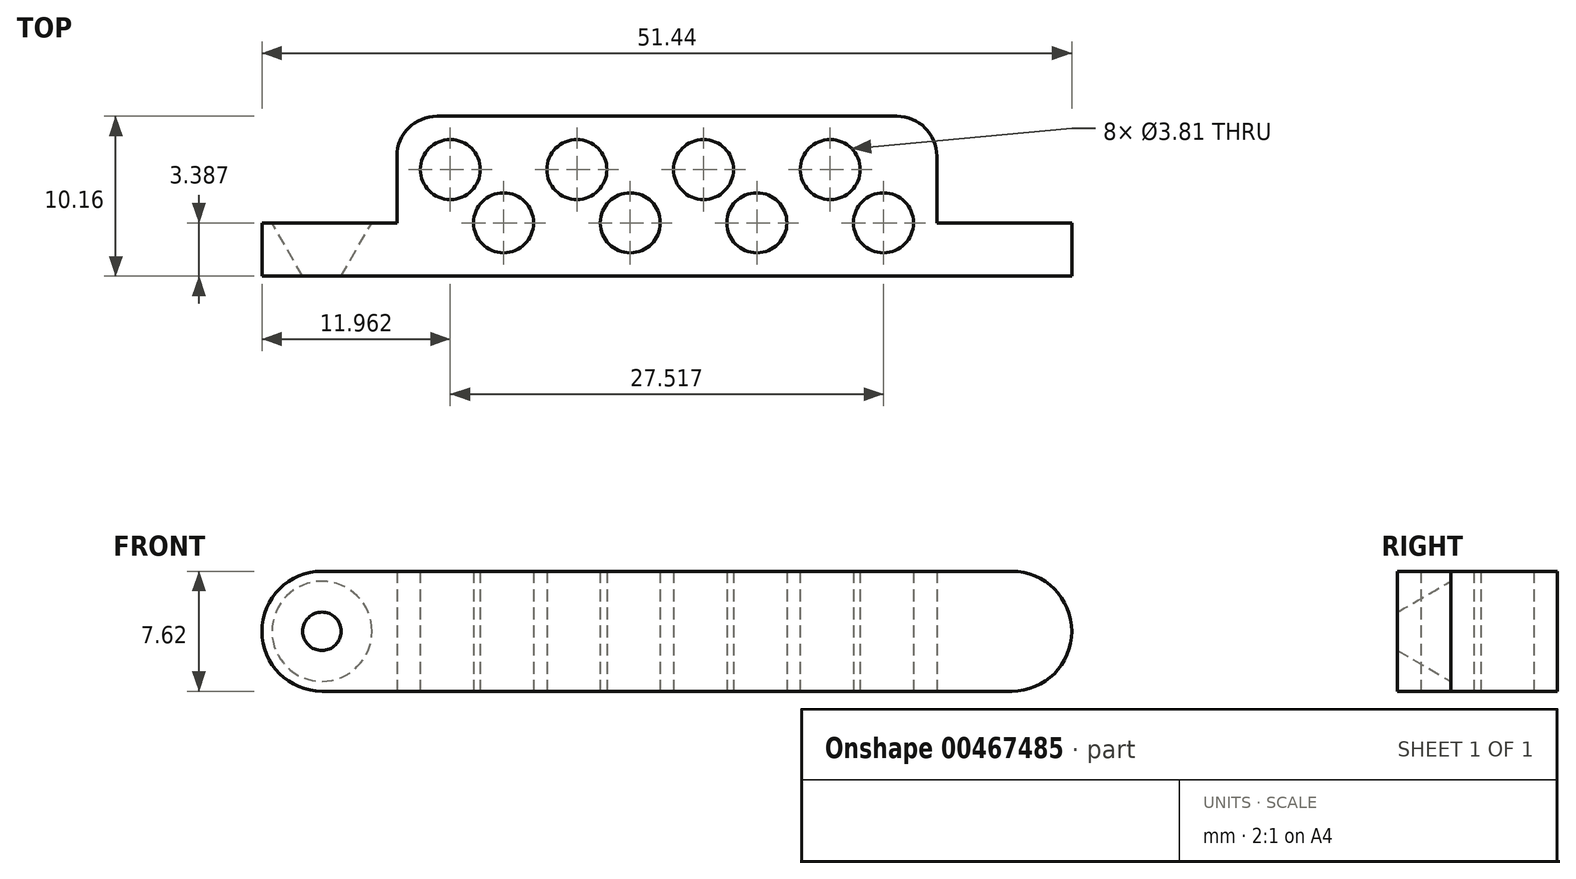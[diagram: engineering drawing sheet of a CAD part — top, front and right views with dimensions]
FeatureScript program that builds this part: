
annotation { "Feature Type Name" : "Feature", "Feature Type Description" : "" }
export const myFeature = defineFeature(function(context is Context, id is Id, definition is map)
    precondition{}
    {
        {
            var Q0;
            Q0=qCreatedBy(makeId("Top.planeOp"),FACE);
            var sketch = newSketch(context, id + "F0", { "sketchPlane" : qUnion([Q0])});
            skLineSegment(sketch, "E0", {"start": v(0, 10.16) * mm, "end": v(-17.15, 10.16) * mm});
            skLineSegment(sketch, "E1", {"start": v(-17.15, 10.16) * mm, "end": v(-17.14, 3.39) * mm});
            skLineSegment(sketch, "E2", {"start": v(-17.14, 3.39) * mm, "end": v(-25.72, 3.39) * mm});
            skLineSegment(sketch, "E3", {"start": v(-25.72, 3.39) * mm, "end": v(-25.72, 0) * mm});
            skLineSegment(sketch, "E4", {"start": v(-25.72, 0) * mm, "end": v(0, 0) * mm});
            skLineSegment(sketch, "E5.MirrorCS", {"start": v(25.72, 0) * mm, "end": v(0, 0) * mm});
            skLineSegment(sketch, "E6.MirrorCS", {"start": v(25.72, 3.39) * mm, "end": v(25.72, 0) * mm});
            skLineSegment(sketch, "E7.MirrorCS", {"start": v(17.14, 3.39) * mm, "end": v(25.72, 3.39) * mm});
            skLineSegment(sketch, "E8.MirrorCS", {"start": v(0, 10.16) * mm, "end": v(17.15, 10.16) * mm});
            skLineSegment(sketch, "E9.MirrorCS", {"start": v(17.14, 10.16) * mm, "end": v(17.14, 3.39) * mm});
            skSolve(sketch);
        }
        {
            var Q0;
            Q0 = qSketchRegion(id + "F0", true);
            extrude(context, id + "F1", {"entities" : qUnion([Q0]), "endBound" : BoundingType.SYMMETRIC, "depth" : 7.62 * mm});
        }
        {
            var Q0;
            Q0=qCreatedBy(makeId("Top.planeOp"),FACE);
            var sketch = newSketch(context, id + "F2", { "sketchPlane" : qUnion([Q0])});
            skCircle(sketch, "E10", {"center": v(-13.76, 6.77) * mm, "radius": 1.9 * mm});
            skCircle(sketch, "E11", {"center": v(-10.37, 3.39) * mm, "radius": 1.9 * mm});
            skLineSegment(sketch, "E12.0", {"start": v(-17.15, 10.16) * mm, "end": v(17.15, 10.16) * mm, "construction": true});
            skLineSegment(sketch, "E13.0", {"start": v(-17.15, 10.16) * mm, "end": v(-17.14, 3.39) * mm, "construction": true});
            skPoint(sketch, "E14", {"position": v(-13.76, 10.16) * mm});
            skLineSegment(sketch, "E15", {"start": v(-13.76, 6.77) * mm, "end": v(-13.76, 10.16) * mm, "construction": true});
            skLineSegment(sketch, "E16", {"start": v(-10.37, 3.39) * mm, "end": v(-10.37, 0) * mm, "construction": true});
            skLineSegment(sketch, "E17", {"start": v(-13.76, 6.77) * mm, "end": v(-13.76, 3.39) * mm, "construction": true});
            skLineSegment(sketch, "E18", {"start": v(-10.37, 3.39) * mm, "end": v(-13.76, 6.77) * mm, "construction": true});
            skPoint(sketch, "E19", {"position": v(-12.06, 5.08) * mm});
            skCircle(sketch, "E20.1.0.0", {"center": v(-2.33, 3.39) * mm, "radius": 1.9 * mm});
            skPoint(sketch, "E20.1.0.1", {"position": v(-5.72, 10.16) * mm});
            skLineSegment(sketch, "E20.1.0.2", {"start": v(-5.72, 6.77) * mm, "end": v(-5.71, 3.39) * mm, "construction": true});
            skLineSegment(sketch, "E20.1.0.3", {"start": v(-2.33, 3.39) * mm, "end": v(-5.72, 6.77) * mm, "construction": true});
            skPoint(sketch, "E20.1.0.4", {"position": v(-4.02, 5.08) * mm});
            skCircle(sketch, "E20.1.0.5", {"center": v(-5.72, 6.77) * mm, "radius": 1.9 * mm});
            skLineSegment(sketch, "E20.1.0.6", {"start": v(-2.33, 3.39) * mm, "end": v(-2.33, 0) * mm, "construction": true});
            skLineSegment(sketch, "E20.1.0.7", {"start": v(-5.71, 6.77) * mm, "end": v(-5.72, 10.16) * mm, "construction": true});
            skCircle(sketch, "E20.2.0.0", {"center": v(5.72, 3.39) * mm, "radius": 1.9 * mm});
            skPoint(sketch, "E20.2.0.1", {"position": v(2.33, 10.16) * mm});
            skLineSegment(sketch, "E20.2.0.2", {"start": v(2.33, 6.77) * mm, "end": v(2.33, 3.39) * mm, "construction": true});
            skLineSegment(sketch, "E20.2.0.3", {"start": v(5.72, 3.39) * mm, "end": v(2.33, 6.77) * mm, "construction": true});
            skPoint(sketch, "E20.2.0.4", {"position": v(4.02, 5.08) * mm});
            skCircle(sketch, "E20.2.0.5", {"center": v(2.33, 6.77) * mm, "radius": 1.9 * mm});
            skLineSegment(sketch, "E20.2.0.6", {"start": v(5.72, 3.39) * mm, "end": v(5.72, 0) * mm, "construction": true});
            skLineSegment(sketch, "E20.2.0.7", {"start": v(2.33, 6.77) * mm, "end": v(2.33, 10.16) * mm, "construction": true});
            skLineSegment(sketch, "E20.direction1", {"start": v(-10.37, 0) * mm, "end": v(-2.33, 0) * mm, "construction": true});
            skCircle(sketch, "E21.0.3.0", {"center": v(13.76, 3.39) * mm, "radius": 1.9 * mm});
            skPoint(sketch, "E21.2.3.0", {"position": v(10.37, 10.16) * mm});
            skLineSegment(sketch, "E21.3.3.0", {"start": v(10.37, 6.77) * mm, "end": v(10.37, 3.39) * mm, "construction": true});
            skLineSegment(sketch, "E21.6.3.0", {"start": v(13.76, 3.39) * mm, "end": v(10.37, 6.77) * mm, "construction": true});
            skPoint(sketch, "E21.9.3.0", {"position": v(12.06, 5.08) * mm});
            skCircle(sketch, "E21.10.3.0", {"center": v(10.37, 6.77) * mm, "radius": 1.9 * mm});
            skLineSegment(sketch, "E21.12.3.0", {"start": v(13.76, 3.39) * mm, "end": v(13.76, 0) * mm, "construction": true});
            skLineSegment(sketch, "E21.15.3.0", {"start": v(10.37, 6.77) * mm, "end": v(10.37, 10.16) * mm, "construction": true});
            skLineSegment(sketch, "E22", {"start": v(-12.06, 5.08) * mm, "end": v(-4.02, 5.08) * mm, "construction": true});
            skLineSegment(sketch, "E23", {"start": v(4.02, 5.08) * mm, "end": v(-4.02, 5.08) * mm, "construction": true});
            skLineSegment(sketch, "E24", {"start": v(12.06, 5.08) * mm, "end": v(4.02, 5.08) * mm, "construction": true});
            skPoint(sketch, "E25", {"position": v(0, 5.08) * mm});
            skLineSegment(sketch, "E26", {"start": v(-13.76, 6.77) * mm, "end": v(-17.14, 6.77) * mm, "construction": true});
            skSolve(sketch);
        }
        {
            var Q0;
            Q0=makeQuery(id+"F1.opExtrude","CAP_EDGE",EDGE,{"disambiguationData":[OSD([sQuery(id+"F0.wireOp",EDGE,"E3")])],"isStart":false});
            var Q1;
            Q1=makeQuery(id+"F1.opExtrude","CAP_EDGE",EDGE,{"disambiguationData":[OSD([sQuery(id+"F0.wireOp",EDGE,"E3")])],"isStart":true});
            var Q2;
            Q2=makeQuery(id+"F1.opExtrude","CAP_EDGE",EDGE,{"disambiguationData":[OSD([sQuery(id+"F0.wireOp",EDGE,"E6.MirrorCS")])],"isStart":false});
            var Q3;
            Q3=makeQuery(id+"F1.opExtrude","CAP_EDGE",EDGE,{"disambiguationData":[OSD([sQuery(id+"F0.wireOp",EDGE,"E6.MirrorCS")])],"isStart":true});
            fillet(context, id + "F3", {"entities" : qUnion([Q0, Q1, Q2, Q3]), "radius" : 3.8 * mm, "tangentPropagation" : true, "allowEdgeOverflow" : false});
        }
        {
            var Q0;
            Q0=makeQuery(id+"F1.opExtrude","SWEPT_EDGE",EDGE,{"disambiguationData":[OSD([sQuery(id+"F0.wireOp",EDGE,"E0"),sQuery(id+"F0.wireOp",EDGE,"E1")])]});
            var Q1;
            Q1=makeQuery(id+"F1.opExtrude","SWEPT_EDGE",EDGE,{"disambiguationData":[OSD([sQuery(id+"F0.wireOp",EDGE,"E8.MirrorCS"),sQuery(id+"F0.wireOp",EDGE,"E9.MirrorCS")])]});
            fillet(context, id + "F4", {"entities" : qUnion([Q0, Q1]), "radius" : 2.54 * mm, "tangentPropagation" : true, "allowEdgeOverflow" : false});
        }
        {
            var Q0;
            Q0 = qSketchRegion(id + "F2", true);
            extrude(context, id + "F5", {"entities" : qUnion([Q0]), "operationType" : NewBodyOperationType.REMOVE, "endBound" : BoundingType.SYMMETRIC, "depth" : 7.62 * mm});
        }
        {
            var Q0;
            Q0=qCreatedBy(makeId("Top.planeOp"),FACE);
            var sketch = newSketch(context, id + "F6", { "sketchPlane" : qUnion([Q0])});
            skLineSegment(sketch, "E27.0", {"start": v(-21.9, 3.39) * mm, "end": v(-21.9, 0) * mm, "construction": true});
            skLineSegment(sketch, "E28", {"start": v(-21.9, 3.39) * mm, "end": v(-25.08, 3.39) * mm});
            skLineSegment(sketch, "E29", {"start": v(-25.08, 3.39) * mm, "end": v(-21.9, -2.11) * mm});
            skLineSegment(sketch, "E30", {"start": v(-21.9, -2.11) * mm, "end": v(-21.9, 3.39) * mm});
            skSolve(sketch);
        }
        {
            var Q0;
            Q0 = qSketchRegion(id + "F6", true);
            var Q1;
            Q1=sQuery(id+"F6.wireOp",EDGE,"E30");
            revolve(context, id + "F7", {"operationType" : NewBodyOperationType.REMOVE, "entities" : qUnion([Q0]), "axis" : qUnion([Q1]), "revolveType" : RevolveType.FULL, "oppositeDirection" : true});
        }
    });
